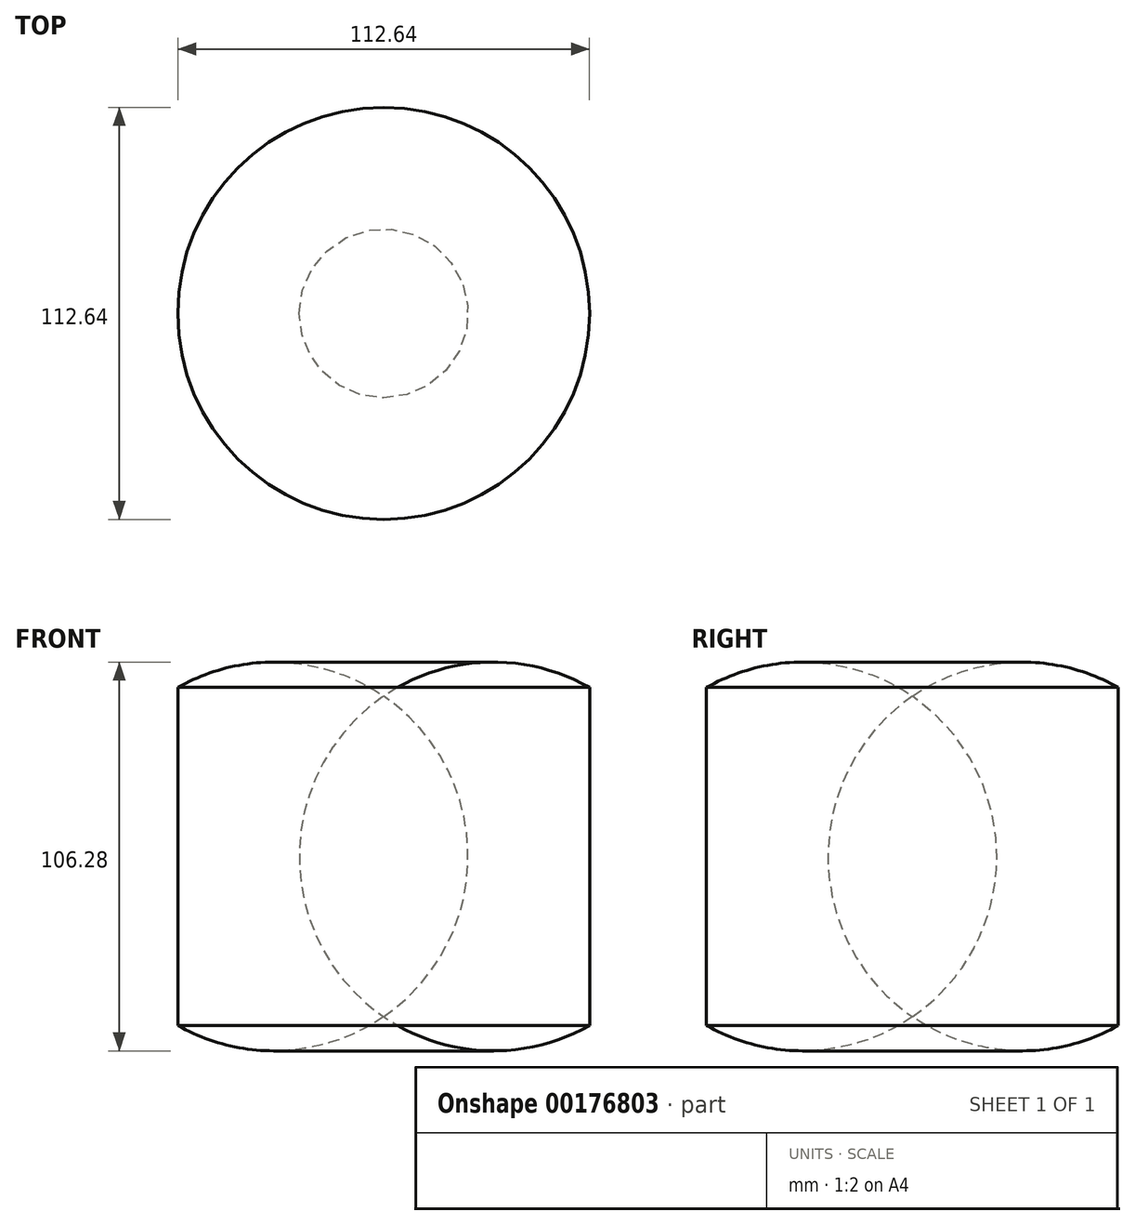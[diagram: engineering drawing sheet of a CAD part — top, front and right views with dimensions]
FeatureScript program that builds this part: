
annotation { "Feature Type Name" : "Feature", "Feature Type Description" : "" }
export const myFeature = defineFeature(function(context is Context, id is Id, definition is map)
    precondition{}
    {
        {
            var Q0;
            Q0=qCreatedBy(makeId("Front.planeOp"),FACE);
            var sketch = newSketch(context, id + "F0", { "sketchPlane" : qUnion([Q0])});
            skLineSegment(sketch, "E0", {"start": v(-53.49, 55.87) * mm, "end": v(-53.49, -36.2) * mm});
            skLineSegment(sketch, "E1", {"start": v(2.83, 56.17) * mm, "end": v(2.83, -36.2) * mm});
            skArc(sketch, "E2", {"start": v(2.83, -36.2) * mm, "mid": v(29.7, 9.98) * mm, "end": v(2.83, 56.17) * mm});
            skSolve(sketch);
        }
        {
            var Q0;
            Q0=makeQuery(id+"F0.imprint","IMPRINT",FACE,{"disambiguationData":[TD([[makeQuery(id+"F0.imprint","IMPRINT",EDGE,{"derivedFrom":sQuery(id+"F0.wireOp",EDGE,"E1")}),1.0]])]});
            var Q1;
            Q1=sQuery(id+"F0.wireOp",EDGE,"E0");
            revolve(context, id + "F1", {"entities" : qUnion([Q0]), "axis" : qUnion([Q1]), "revolveType" : RevolveType.FULL});
        }
    });
